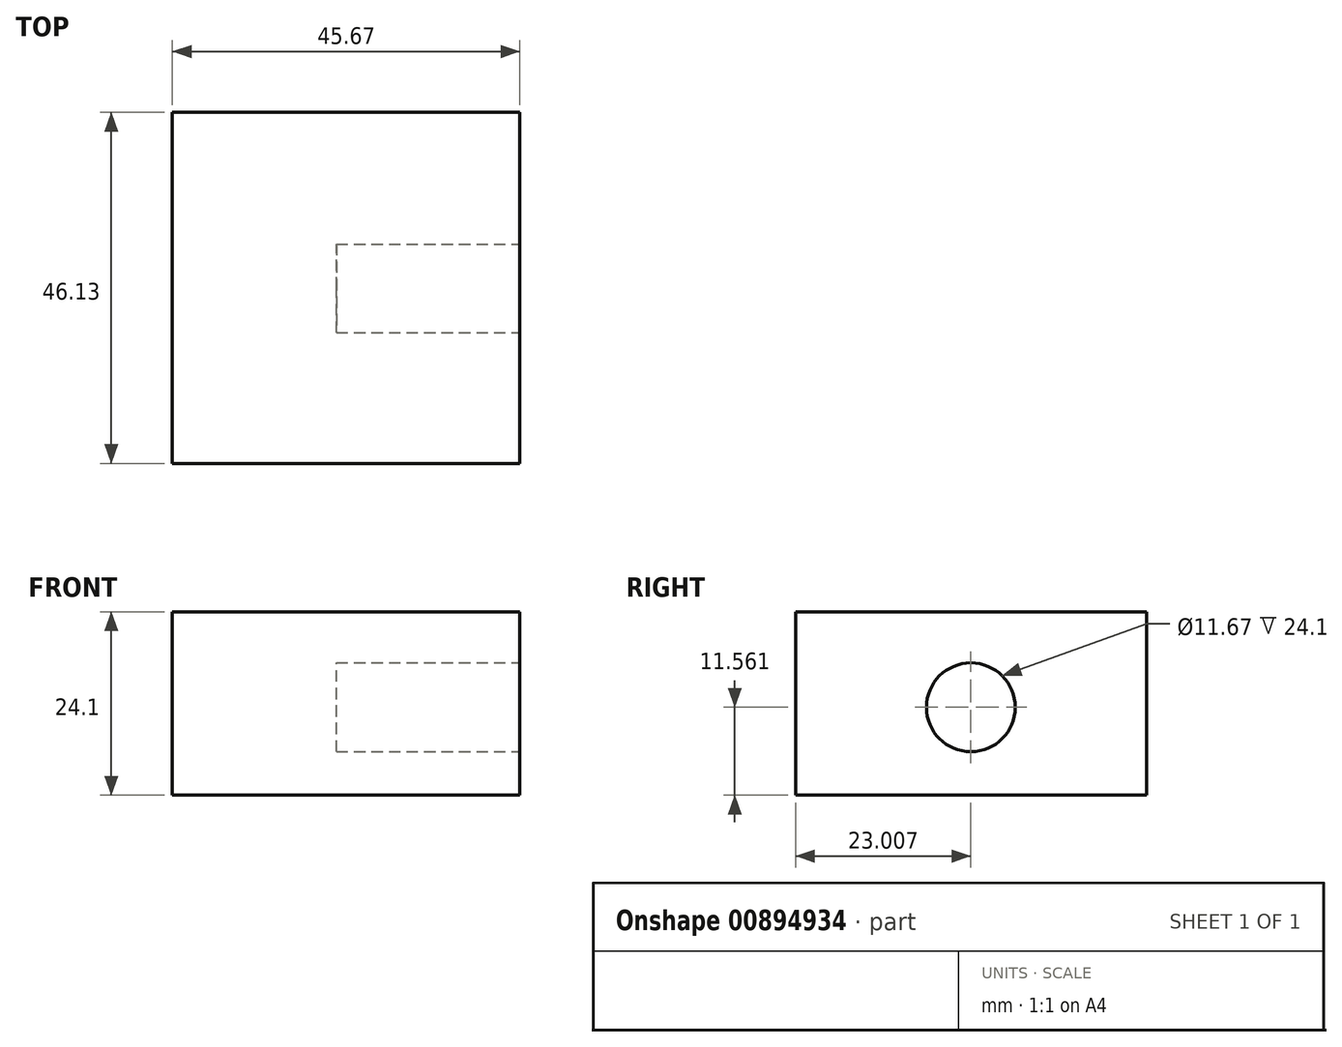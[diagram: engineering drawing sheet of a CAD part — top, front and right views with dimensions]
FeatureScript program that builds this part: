
annotation { "Feature Type Name" : "Feature", "Feature Type Description" : "" }
export const myFeature = defineFeature(function(context is Context, id is Id, definition is map)
    precondition{}
    {
        {
            var Q0;
            Q0=qCreatedBy(makeId("Top.planeOp"),FACE);
            var sketch = newSketch(context, id + "F0", { "sketchPlane" : qUnion([Q0])});
            skLineSegment(sketch, "E0.bottom", {"start": v(0, 0) * mm, "end": v(-45.67, 0) * mm});
            skLineSegment(sketch, "E0.top", {"start": v(0, 46.13) * mm, "end": v(-45.67, 46.13) * mm});
            skLineSegment(sketch, "E0.left", {"start": v(0, 0) * mm, "end": v(0, 46.13) * mm});
            skLineSegment(sketch, "E0.right", {"start": v(-45.67, 0) * mm, "end": v(-45.67, 46.13) * mm});
            skSolve(sketch);
        }
        {
            var Q0;
            Q0 = qSketchRegion(id + "F0", true);
            extrude(context, id + "F1", {"entities" : qUnion([Q0]), "depth" : 24.1 * mm, "offsetDistance" : 25 * mm});
        }
        {
            var Q0;
            Q0=qCreatedBy(makeId("Right.planeOp"),FACE);
            var sketch = newSketch(context, id + "F2", { "sketchPlane" : qUnion([Q0])});
            skCircle(sketch, "E1", {"center": v(23, 11.56) * mm, "radius": 5.84 * mm});
            skSolve(sketch);
        }
        {
            var Q0;
            Q0 = qSketchRegion(id + "F2", true);
            extrude(context, id + "F3", {"entities" : qUnion([Q0]), "operationType" : NewBodyOperationType.REMOVE, "oppositeDirection" : true, "depth" : 24.1 * mm, "offsetDistance" : 25 * mm});
        }
    });
